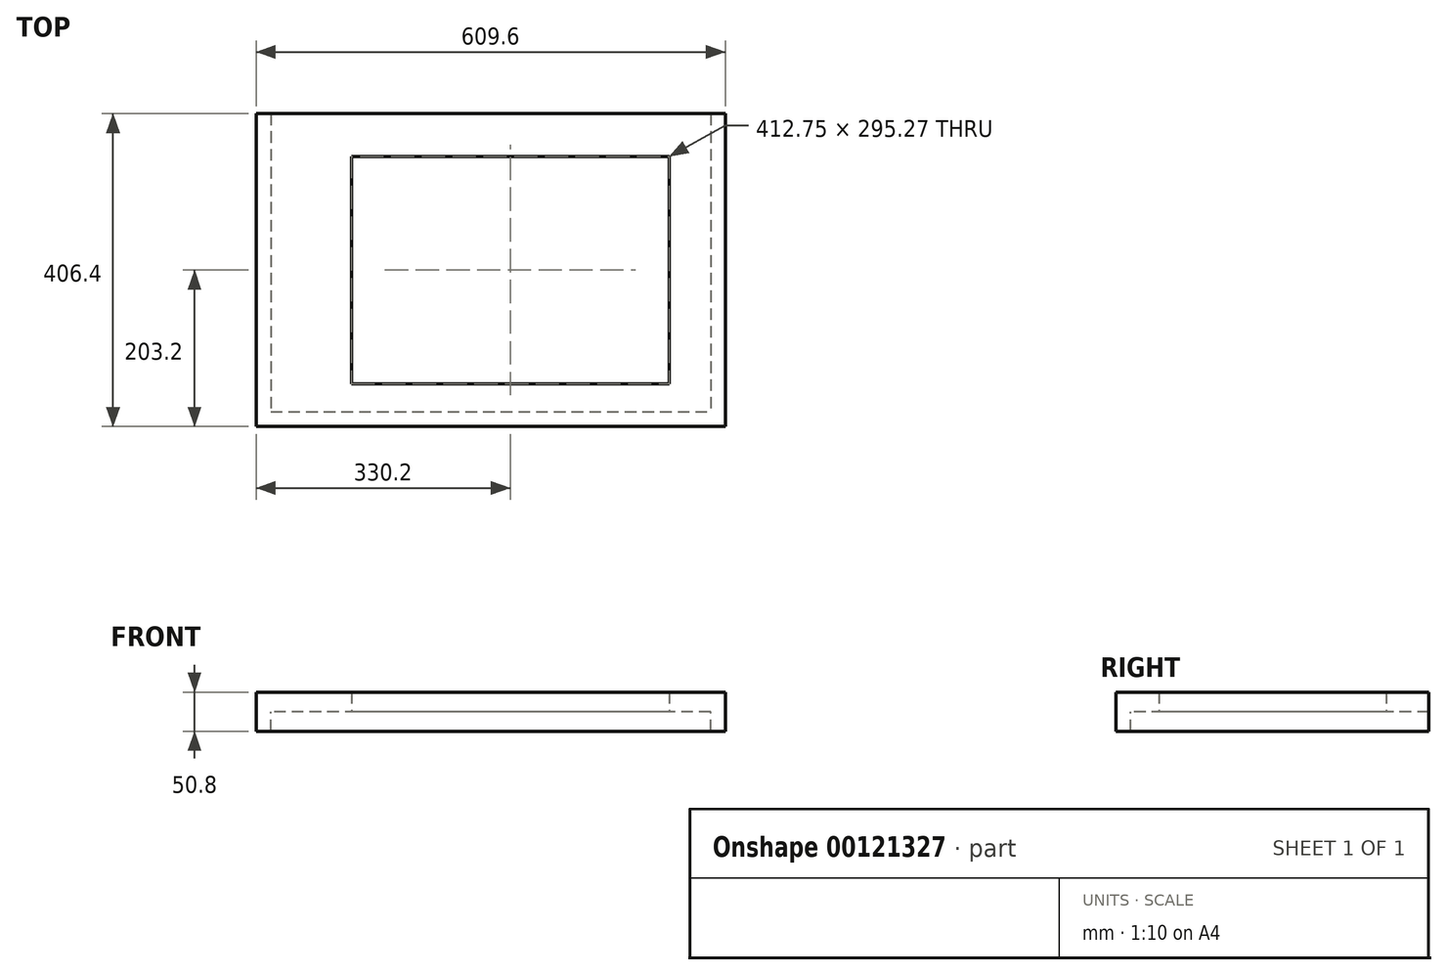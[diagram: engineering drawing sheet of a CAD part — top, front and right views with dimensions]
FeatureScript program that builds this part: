
annotation { "Feature Type Name" : "Feature", "Feature Type Description" : "" }
export const myFeature = defineFeature(function(context is Context, id is Id, definition is map)
    precondition{}
    {
        {
            var Q0;
            Q0=qCreatedBy(makeId("Top.planeOp"),FACE);
            var sketch = newSketch(context, id + "F0", { "sketchPlane" : qUnion([Q0])});
            skLineSegment(sketch, "E0.bottom", {"start": v(279.4, 203.2) * mm, "end": v(-279.4, 203.2) * mm});
            skLineSegment(sketch, "E0.top", {"start": v(279.4, -203.2) * mm, "end": v(-279.4, -203.2) * mm});
            skLineSegment(sketch, "E0.left", {"start": v(279.4, 203.2) * mm, "end": v(279.4, -203.2) * mm});
            skLineSegment(sketch, "E0.right", {"start": v(-279.4, 203.2) * mm, "end": v(-279.4, -203.2) * mm, "construction": true});
            skPoint(sketch, "E0.middle", {"position": v(0, 0) * mm});
            skLineSegment(sketch, "E1.bottom", {"start": v(206.38, 147.64) * mm, "end": v(-206.38, 147.64) * mm});
            skLineSegment(sketch, "E1.top", {"start": v(206.38, -147.64) * mm, "end": v(-206.38, -147.64) * mm});
            skLineSegment(sketch, "E1.left", {"start": v(206.38, 147.64) * mm, "end": v(206.38, -147.64) * mm});
            skLineSegment(sketch, "E1.right", {"start": v(-206.38, 147.64) * mm, "end": v(-206.38, -147.64) * mm});
            skLineSegment(sketch, "E2.bottom", {"start": v(-279.4, -203.2) * mm, "end": v(-330.2, -203.2) * mm});
            skLineSegment(sketch, "E2.top", {"start": v(-279.4, 203.2) * mm, "end": v(-330.2, 203.2) * mm});
            skLineSegment(sketch, "E2.right", {"start": v(-330.2, -203.2) * mm, "end": v(-330.2, 203.2) * mm});
            skSolve(sketch);
        }
        {
            var Q0;
            Q0=makeQuery(id+"F0.imprint","IMPRINT",FACE,{"disambiguationData":[TD([[makeQuery(id+"F0.imprint","IMPRINT",EDGE,{"derivedFrom":sQuery(id+"F0.wireOp",EDGE,"E0.bottom")}),1.0]])]});
            extrude(context, id + "F1", {"entities" : qUnion([Q0]), "depth" : 25.4 * mm});
        }
        {
            var Q0;
            Q0=makeQuery(id+"F1.opExtrude","CAP_FACE",FACE,{"disambiguationData":[OSD([sQuery(id+"F0.wireOp",EDGE,"E0.bottom"),sQuery(id+"F0.wireOp",EDGE,"E0.top"),sQuery(id+"F0.wireOp",EDGE,"E0.left"),sQuery(id+"F0.wireOp",EDGE,"E1.bottom"),sQuery(id+"F0.wireOp",EDGE,"E1.top"),sQuery(id+"F0.wireOp",EDGE,"E1.left"),sQuery(id+"F0.wireOp",EDGE,"E1.right"),sQuery(id+"F0.wireOp",EDGE,"E2.bottom"),sQuery(id+"F0.wireOp",EDGE,"E2.top"),sQuery(id+"F0.wireOp",EDGE,"E2.right")])],"isStart":true});
            var sketch = newSketch(context, id + "F2", { "sketchPlane" : qUnion([Q0])});
            skLineSegment(sketch, "E3.bottom", {"start": v(-330.2, 203.2) * mm, "end": v(279.4, 203.2) * mm});
            skLineSegment(sketch, "E3.top", {"start": v(-330.2, 184.15) * mm, "end": v(279.4, 184.15) * mm});
            skLineSegment(sketch, "E3.left", {"start": v(-330.2, 203.2) * mm, "end": v(-330.2, 184.15) * mm});
            skLineSegment(sketch, "E3.right", {"start": v(279.4, 203.2) * mm, "end": v(279.4, 184.15) * mm});
            skLineSegment(sketch, "E4.bottom", {"start": v(-330.2, -203.2) * mm, "end": v(-311.15, -203.2) * mm});
            skLineSegment(sketch, "E4.top", {"start": v(-330.2, 184.15) * mm, "end": v(-311.15, 184.15) * mm});
            skLineSegment(sketch, "E4.left", {"start": v(-330.2, -203.2) * mm, "end": v(-330.2, 184.15) * mm});
            skLineSegment(sketch, "E4.right", {"start": v(-311.15, -203.2) * mm, "end": v(-311.15, 184.15) * mm});
            skLineSegment(sketch, "E5.bottom", {"start": v(279.4, -203.2) * mm, "end": v(260.35, -203.2) * mm});
            skLineSegment(sketch, "E5.top", {"start": v(279.4, 184.15) * mm, "end": v(260.35, 184.15) * mm});
            skLineSegment(sketch, "E5.left", {"start": v(279.4, -203.2) * mm, "end": v(279.4, 184.15) * mm});
            skLineSegment(sketch, "E5.right", {"start": v(260.35, -203.2) * mm, "end": v(260.35, 184.15) * mm});
            skSolve(sketch);
        }
        {
            var Q0;
            Q0=makeQuery(id+"F2.imprint","IMPRINT",FACE,{"disambiguationData":[TD([[makeQuery(id+"F2.imprint","IMPRINT",EDGE,{"derivedFrom":sQuery(id+"F2.wireOp",EDGE,"E3.bottom")}),1.0]])]});
            var Q1;
            Q1=makeQuery(id+"F2.imprint","IMPRINT",FACE,{"disambiguationData":[TD([[makeQuery(id+"F2.imprint","IMPRINT",EDGE,{"derivedFrom":sQuery(id+"F2.wireOp",EDGE,"E5.bottom")}),-1.0]])]});
            var Q2;
            Q2=makeQuery(id+"F2.imprint","IMPRINT",FACE,{"disambiguationData":[TD([[makeQuery(id+"F2.imprint","IMPRINT",EDGE,{"derivedFrom":sQuery(id+"F2.wireOp",EDGE,"E4.bottom")}),-1.0]])]});
            extrude(context, id + "F3", {"entities" : qUnion([Q0, Q1, Q2]), "operationType" : NewBodyOperationType.ADD, "depth" : 25.4 * mm});
        }
    });
